# Revit family: REVIT-TPO
name_source: partatom
category: Mechanical Equipment
revit_build: Autodesk Revit 2017 (Build: 20190507_1515(x64)
units: mm (PartAtom-declared; Revit-internal decimal feet)

## family parameters
Always vertical = Yes
Cut with Voids When Loaded = No
Part Type = Normal
Room Calculation Point = No
Round Connector Dimension = Use Radius
Shared = No
Work Plane-Based = No

## types (39) — shared parameters
A = 8 3/8"
Air Inlet Depth = 3 1/8"
Air Inlet Extension = 18 15/16"
Air Inlet Width = 6 3/8"
Air Inlet X = 14 7/8"
Air Inlet Y = 5 1/4"
Air Inlet Y Offset = 2 1/16"
Air Inlet Z Offset = 2 1/16"
Assembly Code = D3040400
B = 3 15/16"
Burner Depth = 15 1/2"
Burner Height = 13 3/4"
Burner Width = 14 11/16"
Description = PVI Turbopower - Water Heater
Disclaimer = This rendering is for building modeling purposes only. Submittal/catalog is still the contract document. PVI reserves the right to change design and specification without notice.
Drain Angle = 0.00°
Energy Radius = 14 1/2"
Flue Collector Radius = 11 1/4"
Flue Extension = 18 1/4"
Manufacturer = PVI Industries, LLC
Oil Conn Angle = 90.00°
Oil Inlet NPT = 1/2"
Oil Inlet Radius = 1/4"
Oil Inlet X = 6 15/16"
Oil Inlet Y = 4 5/16"
Oil Inlet Z = 11"
Oil Pump Angle = 0.00°
Rear Access Extension = 0"
Relief Angle = 45.00°
Relief Valve NPT = 3/4"
Relief Valve Radius = 3/8"
URL = www.pvi.com
Voltage = 120 V

## per-type parameters (varying)
- 1500 L 1500A-TPO: Air Inlet Diameter=8"; Air Inlet Radius=4"; Cold Water Extension=38 1/2"; Cold Water NPT=3"; Cold Water Radius=1 1/2"; Control Panel Extension=44 1/2"; Drain Extension=41 3/8"; Drain NPT=1 1/2"; Drain Radius=3/4"; Enclosure Location=30"; Energy Extension=44 1/2"; FC OAL=60"; Flat Side Distance=75"; Flue Collector Extension=15 1/2"; Flue Diameter=8"; Flue Location=52 1/4"; Flue Radius=4"; Front Skid Extension=112 1/2"; Height to Cold Inlet=20"; Height to Drain=2 1/4"; Height to Energy=32 3/8"; Height to Hot Outlet=84 1/2"; Height to Relief=85 1/8"; Hot Outlet Angle=90.00°; Hot Water Extension=38 1/2"; Hot Water NPT=3"; Hot Water Radius=1 1/2"; Input Btu/h=1200000; Input gph Fuel Oil=8.6; Rear Skid Extension=37 1/2"; Recovery Rate 40F to 140F=1200 gph; Relief Extension=40 1/2"; Skid Center Dist=21 1/2"; Skid Length=75"; Skid Spacing=43"; Unit Height=104 1/2"; Unit Radius=37 1/2"
- 1250 L 1500A-TPO: Air Inlet Diameter=8"; Air Inlet Radius=4"; Cold Water Extension=38 1/2"; Cold Water NPT=3"; Cold Water Radius=1 1/2"; Control Panel Extension=44 1/2"; Drain Extension=41 3/8"; Drain NPT=1 1/2"; Drain Radius=3/4"; Enclosure Location=30"; Energy Extension=44 1/2"; FC OAL=60"; Flat Side Distance=75"; Flue Collector Extension=15 1/2"; Flue Diameter=8"; Flue Location=52 1/4"; Flue Radius=4"; Front Skid Extension=112 1/2"; Height to Cold Inlet=20"; Height to Drain=2 1/4"; Height to Energy=32 3/8"; Height to Hot Outlet=84 1/2"; Height to Relief=85 1/8"; Hot Outlet Angle=90.00°; Hot Water Extension=38 1/2"; Hot Water NPT=3"; Hot Water Radius=1 1/2"; Input Btu/h=1000000; Input gph Fuel Oil=7.2; Rear Skid Extension=37 1/2"; Recovery Rate 40F to 140F=1000 gph; Relief Extension=40 1/2"; Skid Center Dist=21 1/2"; Skid Length=75"; Skid Spacing=43"; Unit Height=104 1/2"; Unit Radius=37 1/2"
- 1000 L 1500A-TPO: Air Inlet Diameter=8"; Air Inlet Radius=4"; Cold Water Extension=38 1/2"; Cold Water NPT=3"; Cold Water Radius=1 1/2"; Control Panel Extension=44 1/2"; Drain Extension=41 3/8"; Drain NPT=1 1/2"; Drain Radius=3/4"; Enclosure Location=30"; Energy Extension=43 3/4"; FC OAL=52"; Flat Side Distance=75"; Flue Collector Extension=8 1/4"; Flue Diameter=8"; Flue Location=47 7/8"; Flue Radius=4"; Front Skid Extension=112 1/2"; Height to Cold Inlet=20"; Height to Drain=2 1/4"; Height to Energy=32 3/8"; Height to Hot Outlet=84 1/2"; Height to Relief=85 1/8"; Hot Outlet Angle=90.00°; Hot Water Extension=38 1/2"; Hot Water NPT=3"; Hot Water Radius=1 1/2"; Input Btu/h=800000; Input gph Fuel Oil=5.7; Rear Skid Extension=37 1/2"; Recovery Rate 40F to 140F=800 gph; Relief Extension=40 1/2"; Skid Center Dist=21 1/2"; Skid Length=75"; Skid Spacing=43"; Unit Height=104 1/2"; Unit Radius=37 1/2"
- 750 L 1500A-TPO: Air Inlet Diameter=6"; Air Inlet Radius=3"; Cold Water Extension=38 1/2"; Cold Water NPT=3"; Cold Water Radius=1 1/2"; Control Panel Extension=44 1/2"; Drain Extension=41 3/8"; Drain NPT=1 1/2"; Drain Radius=3/4"; Enclosure Location=30"; Energy Extension=43 3/4"; FC OAL=52"; Flat Side Distance=75"; Flue Collector Extension=8 1/4"; Flue Diameter=6"; Flue Location=47 7/8"; Flue Radius=3"; Front Skid Extension=112 1/2"; Height to Cold Inlet=20"; Height to Drain=2 1/4"; Height to Energy=32 3/8"; Height to Hot Outlet=84 1/2"; Height to Relief=85 1/8"; Hot Outlet Angle=90.00°; Hot Water Extension=38 1/2"; Hot Water NPT=3"; Hot Water Radius=1 1/2"; Input Btu/h=600000; Input gph Fuel Oil=4.3; Rear Skid Extension=37 1/2"; Recovery Rate 40F to 140F=600 gph; Relief Extension=40 1/2"; Skid Center Dist=21 1/2"; Skid Length=75"; Skid Spacing=43"; Unit Height=104 1/2"; Unit Radius=37 1/2"
- 500 L 1500A-TPO: Air Inlet Diameter=5"; Air Inlet Radius=2 1/2"; Cold Water Extension=38 1/2"; Cold Water NPT=3"; Cold Water Radius=1 1/2"; Control Panel Extension=44 1/2"; Drain Extension=41 3/8"; Drain NPT=1 1/2"; Drain Radius=3/4"; Enclosure Location=30"; Energy Extension=44 3/4"; FC OAL=50"; Flat Side Distance=75"; Flue Collector Extension=5 1/4"; Flue Diameter=5"; Flue Location=47 3/8"; Flue Radius=2 1/2"; Front Skid Extension=112 1/2"; Height to Cold Inlet=20"; Height to Drain=2 1/4"; Height to Energy=32 3/8"; Height to Hot Outlet=84 1/2"; Height to Relief=85 1/8"; Hot Outlet Angle=90.00°; Hot Water Extension=38 1/2"; Hot Water NPT=3"; Hot Water Radius=1 1/2"; Input Btu/h=399000; Input gph Fuel Oil=2.8; Rear Skid Extension=37 1/2"; Recovery Rate 40F to 140F=400 gph; Relief Extension=40 1/2"; Skid Center Dist=21 1/2"; Skid Length=75"; Skid Spacing=43"; Unit Height=104 1/2"; Unit Radius=37 1/2"
- 1500 L 1250A-TPO: Air Inlet Diameter=8"; Air Inlet Radius=4"; Cold Water Extension=38 1/2"; Cold Water NPT=3"; Cold Water Radius=1 1/2"; Control Panel Extension=44 1/2"; Drain Extension=41 3/8"; Drain NPT=1 1/2"; Drain Radius=3/4"; Enclosure Location=18"; Energy Extension=44 1/2"; FC OAL=60"; Flat Side Distance=75"; Flue Collector Extension=15 1/2"; Flue Diameter=8"; Flue Location=52 1/4"; Flue Radius=4"; Front Skid Extension=112 1/2"; Height to Cold Inlet=20"; Height to Drain=2 1/4"; Height to Energy=32 3/8"; Height to Hot Outlet=72 1/2"; Height to Relief=73 1/8"; Hot Outlet Angle=90.00°; Hot Water Extension=38 1/2"; Hot Water NPT=3"; Hot Water Radius=1 1/2"; Input Btu/h=1200000; Input gph Fuel Oil=8.6; Rear Skid Extension=37 1/2"; Recovery Rate 40F to 140F=1200 gph; Relief Extension=40 1/2"; Skid Center Dist=21 1/2"; Skid Length=75"; Skid Spacing=43"; Unit Height=92 1/2"; Unit Radius=37 1/2"
- 1250 L 1250A-TPO: Air Inlet Diameter=8"; Air Inlet Radius=4"; Cold Water Extension=38 1/2"; Cold Water NPT=3"; Cold Water Radius=1 1/2"; Control Panel Extension=44 1/2"; Drain Extension=41 3/8"; Drain NPT=1 1/2"; Drain Radius=3/4"; Enclosure Location=18"; Energy Extension=44 1/2"; FC OAL=60"; Flat Side Distance=75"; Flue Collector Extension=15 1/2"; Flue Diameter=8"; Flue Location=52 1/4"; Flue Radius=4"; Front Skid Extension=112 1/2"; Height to Cold Inlet=20"; Height to Drain=2 1/4"; Height to Energy=32 3/8"; Height to Hot Outlet=72 1/2"; Height to Relief=73 1/8"; Hot Outlet Angle=90.00°; Hot Water Extension=38 1/2"; Hot Water NPT=3"; Hot Water Radius=1 1/2"; Input Btu/h=1000000; Input gph Fuel Oil=7.2; Rear Skid Extension=37 1/2"; Recovery Rate 40F to 140F=1000 gph; Relief Extension=40 1/2"; Skid Center Dist=21 1/2"; Skid Length=75"; Skid Spacing=43"; Unit Height=92 1/2"; Unit Radius=37 1/2"
- 1000 L 1250A-TPO: Air Inlet Diameter=8"; Air Inlet Radius=4"; Cold Water Extension=38 1/2"; Cold Water NPT=3"; Cold Water Radius=1 1/2"; Control Panel Extension=44 1/2"; Drain Extension=41 3/8"; Drain NPT=1 1/2"; Drain Radius=3/4"; Enclosure Location=18"; Energy Extension=43 3/4"; FC OAL=52"; Flat Side Distance=75"; Flue Collector Extension=8 1/4"; Flue Diameter=8"; Flue Location=47 7/8"; Flue Radius=4"; Front Skid Extension=112 1/2"; Height to Cold Inlet=20"; Height to Drain=2 1/4"; Height to Energy=32 3/8"; Height to Hot Outlet=72 1/2"; Height to Relief=73 1/8"; Hot Outlet Angle=90.00°; Hot Water Extension=38 1/2"; Hot Water NPT=3"; Hot Water Radius=1 1/2"; Input Btu/h=800000; Input gph Fuel Oil=5.7; Rear Skid Extension=37 1/2"; Recovery Rate 40F to 140F=800 gph; Relief Extension=40 1/2"; Skid Center Dist=21 1/2"; Skid Length=75"; Skid Spacing=43"; Unit Height=92 1/2"; Unit Radius=37 1/2"
- 750 L 1250A-TPO: Air Inlet Diameter=6"; Air Inlet Radius=3"; Cold Water Extension=38 1/2"; Cold Water NPT=3"; Cold Water Radius=1 1/2"; Control Panel Extension=44 1/2"; Drain Extension=41 3/8"; Drain NPT=1 1/2"; Drain Radius=3/4"; Enclosure Location=18"; Energy Extension=43 3/4"; FC OAL=52"; Flat Side Distance=75"; Flue Collector Extension=8 1/4"; Flue Diameter=6"; Flue Location=47 7/8"; Flue Radius=3"; Front Skid Extension=112 1/2"; Height to Cold Inlet=20"; Height to Drain=2 1/4"; Height to Energy=32 3/8"; Height to Hot Outlet=72 1/2"; Height to Relief=73 1/8"; Hot Outlet Angle=90.00°; Hot Water Extension=38 1/2"; Hot Water NPT=3"; Hot Water Radius=1 1/2"; Input Btu/h=600000; Input gph Fuel Oil=4.3; Rear Skid Extension=37 1/2"; Recovery Rate 40F to 140F=600 gph; Relief Extension=40 1/2"; Skid Center Dist=21 1/2"; Skid Length=75"; Skid Spacing=43"; Unit Height=92 1/2"; Unit Radius=37 1/2"
- 500 L 1250A-TPO: Air Inlet Diameter=5"; Air Inlet Radius=2 1/2"; Cold Water Extension=38 1/2"; Cold Water NPT=3"; Cold Water Radius=1 1/2"; Control Panel Extension=44 1/2"; Drain Extension=41 3/8"; Drain NPT=1 1/2"; Drain Radius=3/4"; Enclosure Location=18"; Energy Extension=44 3/4"; FC OAL=50"; Flat Side Distance=75"; Flue Collector Extension=5 1/4"; Flue Diameter=5"; Flue Location=47 3/8"; Flue Radius=2 1/2"; Front Skid Extension=112 1/2"; Height to Cold Inlet=20"; Height to Drain=2 1/4"; Height to Energy=32 3/8"; Height to Hot Outlet=72 1/2"; Height to Relief=73 1/8"; Hot Outlet Angle=90.00°; Hot Water Extension=38 1/2"; Hot Water NPT=3"; Hot Water Radius=1 1/2"; Input Btu/h=399000; Input gph Fuel Oil=2.8; Rear Skid Extension=37 1/2"; Recovery Rate 40F to 140F=400 gph; Relief Extension=40 1/2"; Skid Center Dist=21 1/2"; Skid Length=75"; Skid Spacing=43"; Unit Height=92 1/2"; Unit Radius=37 1/2"
- 1500 L 900A-TPO: Air Inlet Diameter=8"; Air Inlet Radius=4"; Cold Water Extension=34 1/4"; Cold Water NPT=3"; Cold Water Radius=1 1/2"; Control Panel Extension=40 1/4"; Drain Extension=37 1/8"; Drain NPT=1 1/2"; Drain Radius=3/4"; Enclosure Location=24"; Energy Extension=39"; FC OAL=54 1/2"; Flat Side Distance=66 1/2"; Flue Collector Extension=15 1/2"; Flue Diameter=8"; Flue Location=46 3/4"; Flue Radius=4"; Front Skid Extension=101 1/4"; Height to Cold Inlet=20 3/8"; Height to Drain=2 1/4"; Height to Energy=32 5/8"; Height to Hot Outlet=72 7/8"; Height to Relief=73 1/2"; Hot Outlet Angle=90.00°; Hot Water Extension=34 1/4"; Hot Water NPT=3"; Hot Water Radius=1 1/2"; Input Btu/h=1200000; Input gph Fuel Oil=8.6; Rear Skid Extension=33 1/4"; Recovery Rate 40F to 140F=1200 gph; Relief Extension=36 1/4"; Skid Center Dist=18"; Skid Length=68"; Skid Spacing=36"; Unit Height=93 1/4"; Unit Radius=33 1/4"
- 1250 L 900A-TPO: Air Inlet Diameter=8"; Air Inlet Radius=4"; Cold Water Extension=34 1/4"; Cold Water NPT=3"; Cold Water Radius=1 1/2"; Control Panel Extension=40 1/4"; Drain Extension=37 1/8"; Drain NPT=1 1/2"; Drain Radius=3/4"; Enclosure Location=24"; Energy Extension=39"; FC OAL=54 1/2"; Flat Side Distance=66 1/2"; Flue Collector Extension=15 1/2"; Flue Diameter=8"; Flue Location=46 3/4"; Flue Radius=4"; Front Skid Extension=101 1/4"; Height to Cold Inlet=20 3/8"; Height to Drain=2 1/4"; Height to Energy=32 5/8"; Height to Hot Outlet=72 7/8"; Height to Relief=73 1/2"; Hot Outlet Angle=90.00°; Hot Water Extension=34 1/4"; Hot Water NPT=3"; Hot Water Radius=1 1/2"; Input Btu/h=1000000; Input gph Fuel Oil=7.2; Rear Skid Extension=33 1/4"; Recovery Rate 40F to 140F=1000 gph; Relief Extension=36 1/4"; Skid Center Dist=18"; Skid Length=68"; Skid Spacing=36"; Unit Height=93 1/4"; Unit Radius=33 1/4"
- 1000 L 900A-TPO: Air Inlet Diameter=8"; Air Inlet Radius=4"; Cold Water Extension=34 1/4"; Cold Water NPT=3"; Cold Water Radius=1 1/2"; Control Panel Extension=40 1/4"; Drain Extension=37 1/8"; Drain NPT=1 1/2"; Drain Radius=3/4"; Enclosure Location=24"; Energy Extension=38 1/4"; FC OAL=46 1/2"; Flat Side Distance=66 1/2"; Flue Collector Extension=8 1/4"; Flue Diameter=8"; Flue Location=42 3/8"; Flue Radius=4"; Front Skid Extension=101 1/4"; Height to Cold Inlet=20 3/8"; Height to Drain=2 1/4"; Height to Energy=32 5/8"; Height to Hot Outlet=72 7/8"; Height to Relief=73 1/2"; Hot Outlet Angle=90.00°; Hot Water Extension=34 1/4"; Hot Water NPT=3"; Hot Water Radius=1 1/2"; Input Btu/h=800000; Input gph Fuel Oil=5.7; Rear Skid Extension=33 1/4"; Recovery Rate 40F to 140F=800 gph; Relief Extension=36 1/4"; Skid Center Dist=18"; Skid Length=68"; Skid Spacing=36"; Unit Height=93 1/4"; Unit Radius=33 1/4"
- 750 L 900A-TPO: Air Inlet Diameter=6"; Air Inlet Radius=3"; Cold Water Extension=34 1/4"; Cold Water NPT=3"; Cold Water Radius=1 1/2"; Control Panel Extension=40 1/4"; Drain Extension=37 1/8"; Drain NPT=1 1/2"; Drain Radius=3/4"; Enclosure Location=24"; Energy Extension=38 1/4"; FC OAL=46 1/2"; Flat Side Distance=66 1/2"; Flue Collector Extension=8 1/4"; Flue Diameter=6"; Flue Location=42 3/8"; Flue Radius=3"; Front Skid Extension=101 1/4"; Height to Cold Inlet=20 3/8"; Height to Drain=2 1/4"; Height to Energy=32 5/8"; Height to Hot Outlet=72 7/8"; Height to Relief=73 1/2"; Hot Outlet Angle=90.00°; Hot Water Extension=34 1/4"; Hot Water NPT=3"; Hot Water Radius=1 1/2"; Input Btu/h=600000; Input gph Fuel Oil=4.3; Rear Skid Extension=33 1/4"; Recovery Rate 40F to 140F=600 gph; Relief Extension=36 1/4"; Skid Center Dist=18"; Skid Length=68"; Skid Spacing=36"; Unit Height=93 1/4"; Unit Radius=33 1/4"
- 500 L 900A-TPO: Air Inlet Diameter=5"; Air Inlet Radius=2 1/2"; Cold Water Extension=34 1/4"; Cold Water NPT=3"; Cold Water Radius=1 1/2"; Control Panel Extension=40 1/4"; Drain Extension=37 1/8"; Drain NPT=1 1/2"; Drain Radius=3/4"; Enclosure Location=24"; Energy Extension=38 1/4"; FC OAL=43 1/2"; Flat Side Distance=66 1/2"; Flue Collector Extension=5 1/4"; Flue Diameter=5"; Flue Location=40 7/8"; Flue Radius=2 1/2"; Front Skid Extension=101 1/4"; Height to Cold Inlet=20 3/8"; Height to Drain=2 1/4"; Height to Energy=32 5/8"; Height to Hot Outlet=72 7/8"; Height to Relief=73 1/2"; Hot Outlet Angle=90.00°; Hot Water Extension=34 1/4"; Hot Water NPT=3"; Hot Water Radius=1 1/2"; Input Btu/h=399000; Input gph Fuel Oil=2.8; Rear Skid Extension=33 1/4"; Recovery Rate 40F to 140F=400 gph; Relief Extension=36 1/4"; Skid Center Dist=18"; Skid Length=68"; Skid Spacing=36"; Unit Height=93 1/4"; Unit Radius=33 1/4"
- 1500 L 600A-TPO: Air Inlet Diameter=8"; Air Inlet Radius=4"; Cold Water Extension=28 7/8"; Cold Water NPT=3"; Cold Water Radius=1 1/2"; Control Panel Extension=34 7/8"; Drain Extension=31 3/4"; Drain NPT=1 1/2"; Drain Radius=3/4"; Enclosure Location=19 1/2"; Energy Extension=33 3/8"; FC OAL=48 7/8"; Flat Side Distance=55 3/4"; Flue Collector Extension=15 1/2"; Flue Diameter=8"; Flue Location=41 1/8"; Flue Radius=4"; Front Skid Extension=82 3/8"; Height to Cold Inlet=18 1/4"; Height to Drain=2 1/4"; Height to Energy=30"; Height to Hot Outlet=69 3/8"; Height to Relief=70"; Hot Outlet Angle=90.00°; Hot Water Extension=28 7/8"; Hot Water NPT=3"; Hot Water Radius=1 1/2"; Input Btu/h=1200000; Input gph Fuel Oil=8.6; Rear Skid Extension=27 7/8"; Recovery Rate 40F to 140F=1200 gph; Relief Extension=30 7/8"; Skid Center Dist=13 1/2"; Skid Length=54 1/2"; Skid Spacing=27"; Unit Height=87 3/4"; Unit Radius=27 7/8"
- 1250 L 600A-TPO: Air Inlet Diameter=8"; Air Inlet Radius=4"; Cold Water Extension=28 7/8"; Cold Water NPT=3"; Cold Water Radius=1 1/2"; Control Panel Extension=34 7/8"; Drain Extension=31 3/4"; Drain NPT=1 1/2"; Drain Radius=3/4"; Enclosure Location=19 1/2"; Energy Extension=33 3/8"; FC OAL=48 7/8"; Flat Side Distance=55 3/4"; Flue Collector Extension=15 1/2"; Flue Diameter=8"; Flue Location=41 1/8"; Flue Radius=4"; Front Skid Extension=82 3/8"; Height to Cold Inlet=18 1/4"; Height to Drain=2 1/4"; Height to Energy=30"; Height to Hot Outlet=69 3/8"; Height to Relief=70"; Hot Outlet Angle=90.00°; Hot Water Extension=28 7/8"; Hot Water NPT=3"; Hot Water Radius=1 1/2"; Input Btu/h=1000000; Input gph Fuel Oil=7.2; Rear Skid Extension=27 7/8"; Recovery Rate 40F to 140F=1000 gph; Relief Extension=30 7/8"; Skid Center Dist=13 1/2"; Skid Length=54 1/2"; Skid Spacing=27"; Unit Height=87 3/4"; Unit Radius=27 7/8"
- 1000 L 600A-TPO: Air Inlet Diameter=8"; Air Inlet Radius=4"; Cold Water Extension=28 7/8"; Cold Water NPT=3"; Cold Water Radius=1 1/2"; Control Panel Extension=34 7/8"; Drain Extension=31 3/4"; Drain NPT=1 1/2"; Drain Radius=3/4"; Enclosure Location=19 1/2"; Energy Extension=32 5/8"; FC OAL=40 7/8"; Flat Side Distance=55 3/4"; Flue Collector Extension=8 1/4"; Flue Diameter=8"; Flue Location=36 3/4"; Flue Radius=4"; Front Skid Extension=82 3/8"; Height to Cold Inlet=18 1/4"; Height to Drain=2 1/4"; Height to Energy=30"; Height to Hot Outlet=69 3/8"; Height to Relief=70"; Hot Outlet Angle=90.00°; Hot Water Extension=28 7/8"; Hot Water NPT=3"; Hot Water Radius=1 1/2"; Input Btu/h=800000; Input gph Fuel Oil=5.7; Rear Skid Extension=27 7/8"; Recovery Rate 40F to 140F=800 gph; Relief Extension=30 7/8"; Skid Center Dist=13 1/2"; Skid Length=54 1/2"; Skid Spacing=27"; Unit Height=87 3/4"; Unit Radius=27 7/8"
- 750 L 600A-TPO: Air Inlet Diameter=6"; Air Inlet Radius=3"; Cold Water Extension=28 7/8"; Cold Water NPT=3"; Cold Water Radius=1 1/2"; Control Panel Extension=34 7/8"; Drain Extension=31 3/4"; Drain NPT=1 1/2"; Drain Radius=3/4"; Enclosure Location=19 1/2"; Energy Extension=32 5/8"; FC OAL=40 7/8"; Flat Side Distance=55 3/4"; Flue Collector Extension=8 1/4"; Flue Diameter=6"; Flue Location=36 3/4"; Flue Radius=3"; Front Skid Extension=82 3/8"; Height to Cold Inlet=18 1/4"; Height to Drain=2 1/4"; Height to Energy=30"; Height to Hot Outlet=69 3/8"; Height to Relief=70"; Hot Outlet Angle=90.00°; Hot Water Extension=28 7/8"; Hot Water NPT=3"; Hot Water Radius=1 1/2"; Input Btu/h=600000; Input gph Fuel Oil=4.3; Rear Skid Extension=27 7/8"; Recovery Rate 40F to 140F=600 gph; Relief Extension=30 7/8"; Skid Center Dist=13 1/2"; Skid Length=54 1/2"; Skid Spacing=27"; Unit Height=87 3/4"; Unit Radius=27 7/8"
- 500 L 600A-TPO: Air Inlet Diameter=5"; Air Inlet Radius=2 1/2"; Cold Water Extension=28 7/8"; Cold Water NPT=3"; Cold Water Radius=1 1/2"; Control Panel Extension=34 7/8"; Drain Extension=31 3/4"; Drain NPT=1 1/2"; Drain Radius=3/4"; Enclosure Location=19 1/2"; Energy Extension=32 5/8"; FC OAL=37 7/8"; Flat Side Distance=55 3/4"; Flue Collector Extension=5 1/4"; Flue Diameter=5"; Flue Location=35 1/4"; Flue Radius=2 1/2"; Front Skid Extension=82 3/8"; Height to Cold Inlet=18 1/4"; Height to Drain=2 1/4"; Height to Energy=30"; Height to Hot Outlet=69 3/8"; Height to Relief=70"; Hot Outlet Angle=90.00°; Hot Water Extension=28 7/8"; Hot Water NPT=3"; Hot Water Radius=1 1/2"; Input Btu/h=399000; Input gph Fuel Oil=2.8; Rear Skid Extension=27 7/8"; Recovery Rate 40F to 140F=400 gph; Relief Extension=30 7/8"; Skid Center Dist=13 1/2"; Skid Length=54 1/2"; Skid Spacing=27"; Unit Height=87 3/4"; Unit Radius=27 7/8"
- 1500 L 400A-TPO: Air Inlet Diameter=8"; Air Inlet Radius=4"; Cold Water Extension=23 5/8"; Cold Water NPT=2"; Cold Water Radius=1"; Control Panel Extension=29 5/8"; Drain Extension=26 1/2"; Drain NPT=1"; Drain Radius=1/2"; Enclosure Location=15"; Energy Extension=38 1/8"; FC OAL=53 5/8"; Flat Side Distance=45 1/4"; Flue Collector Extension=15 1/2"; Flue Diameter=8"; Flue Location=45 7/8"; Flue Radius=4"; Front Skid Extension=77 1/8"; Height to Cold Inlet=17 1/16"; Height to Drain=1 7/8"; Height to Energy=28 3/4"; Height to Hot Outlet=68 1/2"; Height to Relief=69 1/8"; Hot Outlet Angle=90.00°; Hot Water Extension=23 5/8"; Hot Water NPT=2"; Hot Water Radius=1"; Input Btu/h=1200000; Input gph Fuel Oil=8.6; Rear Skid Extension=22 5/8"; Recovery Rate 40F to 140F=1200 gph; Relief Extension=25 5/8"; Skid Center Dist=13 1/2"; Skid Length=54 1/2"; Skid Spacing=27"; Unit Height=85 1/2"; Unit Radius=22 5/8"
- 1250 L 400A-TPO: Air Inlet Diameter=8"; Air Inlet Radius=4"; Cold Water Extension=23 5/8"; Cold Water NPT=2"; Cold Water Radius=1"; Control Panel Extension=29 5/8"; Drain Extension=26 1/2"; Drain NPT=1"; Drain Radius=1/2"; Enclosure Location=15"; Energy Extension=38 1/8"; FC OAL=53 5/8"; Flat Side Distance=45 1/4"; Flue Collector Extension=15 1/2"; Flue Diameter=8"; Flue Location=45 7/8"; Flue Radius=4"; Front Skid Extension=77 1/8"; Height to Cold Inlet=17 1/16"; Height to Drain=1 7/8"; Height to Energy=28 3/4"; Height to Hot Outlet=68 1/2"; Height to Relief=69 1/8"; Hot Outlet Angle=90.00°; Hot Water Extension=23 5/8"; Hot Water NPT=2"; Hot Water Radius=1"; Input Btu/h=1000000; Input gph Fuel Oil=7.2; Rear Skid Extension=22 5/8"; Recovery Rate 40F to 140F=1000 gph; Relief Extension=25 5/8"; Skid Center Dist=13 1/2"; Skid Length=54 1/2"; Skid Spacing=27"; Unit Height=85 1/2"; Unit Radius=22 5/8"
- 1000 L 400A-TPO: Air Inlet Diameter=8"; Air Inlet Radius=4"; Cold Water Extension=23 5/8"; Cold Water NPT=2"; Cold Water Radius=1"; Control Panel Extension=29 5/8"; Drain Extension=26 1/2"; Drain NPT=1"; Drain Radius=1/2"; Enclosure Location=15"; Energy Extension=27 1/8"; FC OAL=35 3/8"; Flat Side Distance=45 1/4"; Flue Collector Extension=8 1/4"; Flue Diameter=8"; Flue Location=31 1/4"; Flue Radius=4"; Front Skid Extension=68 5/8"; Height to Cold Inlet=17 1/16"; Height to Drain=1 7/8"; Height to Energy=28 3/4"; Height to Hot Outlet=68 1/2"; Height to Relief=69 1/8"; Hot Outlet Angle=90.00°; Hot Water Extension=23 5/8"; Hot Water NPT=2"; Hot Water Radius=1"; Input Btu/h=800000; Input gph Fuel Oil=5.7; Rear Skid Extension=22 5/8"; Recovery Rate 40F to 140F=800 gph; Relief Extension=25 5/8"; Skid Center Dist=13 1/2"; Skid Length=46"; Skid Spacing=27"; Unit Height=85 1/2"; Unit Radius=22 5/8"
- 750 L 400A-TPO: Air Inlet Diameter=6"; Air Inlet Radius=3"; Cold Water Extension=23 5/8"; Cold Water NPT=2"; Cold Water Radius=1"; Control Panel Extension=29 5/8"; Drain Extension=26 1/2"; Drain NPT=1"; Drain Radius=1/2"; Enclosure Location=15"; Energy Extension=27 1/8"; FC OAL=35 3/8"; Flat Side Distance=45 1/4"; Flue Collector Extension=8 1/4"; Flue Diameter=6"; Flue Location=31 1/4"; Flue Radius=3"; Front Skid Extension=68 5/8"; Height to Cold Inlet=17 1/16"; Height to Drain=1 7/8"; Height to Energy=28 3/4"; Height to Hot Outlet=68 1/2"; Height to Relief=69 1/8"; Hot Outlet Angle=90.00°; Hot Water Extension=23 5/8"; Hot Water NPT=2"; Hot Water Radius=1"; Input Btu/h=600000; Input gph Fuel Oil=4.3; Rear Skid Extension=22 5/8"; Recovery Rate 40F to 140F=600 gph; Relief Extension=25 5/8"; Skid Center Dist=13 1/2"; Skid Length=46"; Skid Spacing=27"; Unit Height=85 1/2"; Unit Radius=22 5/8"
- 500 L 400A-TPO: Air Inlet Diameter=5"; Air Inlet Radius=2 1/2"; Cold Water Extension=23 5/8"; Cold Water NPT=2"; Cold Water Radius=1"; Control Panel Extension=29 5/8"; Drain Extension=26 1/2"; Drain NPT=1"; Drain Radius=1/2"; Enclosure Location=15"; Energy Extension=27 1/8"; FC OAL=32 3/8"; Flat Side Distance=45 1/4"; Flue Collector Extension=5 1/4"; Flue Diameter=5"; Flue Location=29 3/4"; Flue Radius=2 1/2"; Front Skid Extension=68 5/8"; Height to Cold Inlet=17 1/16"; Height to Drain=1 7/8"; Height to Energy=28 3/4"; Height to Hot Outlet=68 1/2"; Height to Relief=69 1/8"; Hot Outlet Angle=90.00°; Hot Water Extension=23 5/8"; Hot Water NPT=2"; Hot Water Radius=1"; Input Btu/h=399000; Input gph Fuel Oil=2.8; Rear Skid Extension=22 5/8"; Recovery Rate 40F to 140F=400 gph; Relief Extension=25 5/8"; Skid Center Dist=13 1/2"; Skid Length=46"; Skid Spacing=27"; Unit Height=85 1/2"; Unit Radius=22 5/8"
- 1500 L 250A-TPO: Air Inlet Diameter=8"; Air Inlet Radius=4"; Cold Water Extension=23 5/8"; Cold Water NPT=2"; Cold Water Radius=1"; Control Panel Extension=29 5/8"; Drain Extension=26 1/2"; Drain NPT=1"; Drain Radius=1/2"; Enclosure Location=1 1/2"; Energy Extension=38 1/8"; FC OAL=53 5/8"; Flat Side Distance=45 1/4"; Flue Collector Extension=15 1/2"; Flue Diameter=8"; Flue Location=45 7/8"; Flue Radius=4"; Front Skid Extension=77 1/8"; Height to Cold Inlet=17 1/16"; Height to Drain=1 7/8"; Height to Energy=28 3/4"; Height to Hot Outlet=38 7/8"; Height to Relief=45 1/8"; Hot Outlet Angle=0.00°; Hot Water Extension=23 5/8"; Hot Water NPT=2"; Hot Water Radius=1"; Input Btu/h=1200000; Input gph Fuel Oil=8.6; Rear Skid Extension=22 5/8"; Recovery Rate 40F to 140F=1200 gph; Relief Extension=25 5/8"; Skid Center Dist=13 1/2"; Skid Length=54 1/2"; Skid Spacing=27"; Unit Height=61 1/2"; Unit Radius=22 5/8"
- 1250 L 250A-TPO: Air Inlet Diameter=8"; Air Inlet Radius=4"; Cold Water Extension=23 5/8"; Cold Water NPT=2"; Cold Water Radius=1"; Control Panel Extension=29 5/8"; Drain Extension=26 1/2"; Drain NPT=1"; Drain Radius=1/2"; Enclosure Location=1 1/2"; Energy Extension=38 1/8"; FC OAL=53 5/8"; Flat Side Distance=45 1/4"; Flue Collector Extension=15 1/2"; Flue Diameter=8"; Flue Location=45 7/8"; Flue Radius=4"; Front Skid Extension=77 1/8"; Height to Cold Inlet=17 1/16"; Height to Drain=1 7/8"; Height to Energy=28 3/4"; Height to Hot Outlet=38 7/8"; Height to Relief=45 1/8"; Hot Outlet Angle=0.00°; Hot Water Extension=23 5/8"; Hot Water NPT=2"; Hot Water Radius=1"; Input Btu/h=1000000; Input gph Fuel Oil=7.2; Rear Skid Extension=22 5/8"; Recovery Rate 40F to 140F=1000 gph; Relief Extension=25 5/8"; Skid Center Dist=13 1/2"; Skid Length=54 1/2"; Skid Spacing=27"; Unit Height=61 1/2"; Unit Radius=22 5/8"
- 1000 L 250A-TPO: Air Inlet Diameter=8"; Air Inlet Radius=4"; Cold Water Extension=23 5/8"; Cold Water NPT=2"; Cold Water Radius=1"; Control Panel Extension=29 5/8"; Drain Extension=26 1/2"; Drain NPT=1"; Drain Radius=1/2"; Enclosure Location=1 1/2"; Energy Extension=27 1/8"; FC OAL=35 3/8"; Flat Side Distance=45 1/4"; Flue Collector Extension=8 1/4"; Flue Diameter=8"; Flue Location=31 1/4"; Flue Radius=4"; Front Skid Extension=68 5/8"; Height to Cold Inlet=17 1/16"; Height to Drain=1 7/8"; Height to Energy=28 3/4"; Height to Hot Outlet=38 7/8"; Height to Relief=45 1/8"; Hot Outlet Angle=0.00°; Hot Water Extension=23 5/8"; Hot Water NPT=2"; Hot Water Radius=1"; Input Btu/h=800000; Input gph Fuel Oil=5.7; Rear Skid Extension=22 5/8"; Recovery Rate 40F to 140F=800 gph; Relief Extension=25 5/8"; Skid Center Dist=13 1/2"; Skid Length=46"; Skid Spacing=27"; Unit Height=61 1/2"; Unit Radius=22 5/8"
- 750 L 250A-TPO: Air Inlet Diameter=6"; Air Inlet Radius=3"; Cold Water Extension=23 5/8"; Cold Water NPT=2"; Cold Water Radius=1"; Control Panel Extension=29 5/8"; Drain Extension=26 1/2"; Drain NPT=1"; Drain Radius=1/2"; Enclosure Location=1 1/2"; Energy Extension=27 1/8"; FC OAL=35 3/8"; Flat Side Distance=45 1/4"; Flue Collector Extension=8 1/4"; Flue Diameter=6"; Flue Location=31 1/4"; Flue Radius=3"; Front Skid Extension=68 5/8"; Height to Cold Inlet=17 1/16"; Height to Drain=1 7/8"; Height to Energy=28 3/4"; Height to Hot Outlet=38 7/8"; Height to Relief=45 1/8"; Hot Outlet Angle=0.00°; Hot Water Extension=23 5/8"; Hot Water NPT=2"; Hot Water Radius=1"; Input Btu/h=600000; Input gph Fuel Oil=4.3; Rear Skid Extension=22 5/8"; Recovery Rate 40F to 140F=600 gph; Relief Extension=25 5/8"; Skid Center Dist=13 1/2"; Skid Length=46"; Skid Spacing=27"; Unit Height=61 1/2"; Unit Radius=22 5/8"
- 500 L 250A-TPO: Air Inlet Diameter=5"; Air Inlet Radius=2 1/2"; Cold Water Extension=23 5/8"; Cold Water NPT=2"; Cold Water Radius=1"; Control Panel Extension=29 5/8"; Drain Extension=26 1/2"; Drain NPT=1"; Drain Radius=1/2"; Enclosure Location=1 1/2"; Energy Extension=27 1/8"; FC OAL=32 3/8"; Flat Side Distance=45 1/4"; Flue Collector Extension=5 1/4"; Flue Diameter=5"; Flue Location=29 3/4"; Flue Radius=2 1/2"; Front Skid Extension=68 5/8"; Height to Cold Inlet=17 1/16"; Height to Drain=1 7/8"; Height to Energy=28 3/4"; Height to Hot Outlet=38 7/8"; Height to Relief=45 1/8"; Hot Outlet Angle=0.00°; Hot Water Extension=23 5/8"; Hot Water NPT=2"; Hot Water Radius=1"; Input Btu/h=399000; Input gph Fuel Oil=2.8; Rear Skid Extension=22 5/8"; Recovery Rate 40F to 140F=400 gph; Relief Extension=25 5/8"; Skid Center Dist=13 1/2"; Skid Length=46"; Skid Spacing=27"; Unit Height=61 1/2"; Unit Radius=22 5/8"
- 1000 L 215A-TPO: Air Inlet Diameter=8"; Air Inlet Radius=4"; Cold Water Extension=19 1/8"; Cold Water NPT=2"; Cold Water Radius=1"; Control Panel Extension=25 1/8"; Drain Extension=22"; Drain NPT=1"; Drain Radius=1/2"; Enclosure Location=11 3/4"; Energy Extension=37 1/8"; FC OAL=45 3/8"; Flat Side Distance=34"; Flue Collector Extension=8 1/4"; Flue Diameter=8"; Flue Location=41 1/4"; Flue Radius=4"; Front Skid Extension=55 1/8"; Height to Cold Inlet=14 13/16"; Height to Drain=1 7/8"; Height to Energy=26 1/2"; Height to Hot Outlet=64"; Height to Relief=66 5/16"; Hot Outlet Angle=90.00°; Hot Water Extension=19 1/8"; Hot Water NPT=2"; Hot Water Radius=1"; Input Btu/h=800000; Input gph Fuel Oil=5.7; Rear Skid Extension=18 1/8"; Recovery Rate 40F to 140F=800 gph; Relief Extension=21 1/8"; Skid Center Dist=8 1/2"; Skid Length=37"; Skid Spacing=17"; Unit Height=76"; Unit Radius=18 1/8"
- 750 L 215A-TPO: Air Inlet Diameter=6"; Air Inlet Radius=3"; Cold Water Extension=19 1/8"; Cold Water NPT=2"; Cold Water Radius=1"; Control Panel Extension=25 1/8"; Drain Extension=22"; Drain NPT=1"; Drain Radius=1/2"; Enclosure Location=11 3/4"; Energy Extension=37 1/8"; FC OAL=45 3/8"; Flat Side Distance=34"; Flue Collector Extension=8 1/4"; Flue Diameter=6"; Flue Location=41 1/4"; Flue Radius=3"; Front Skid Extension=55 1/8"; Height to Cold Inlet=14 13/16"; Height to Drain=1 7/8"; Height to Energy=26 1/2"; Height to Hot Outlet=64"; Height to Relief=66 5/16"; Hot Outlet Angle=90.00°; Hot Water Extension=19 1/8"; Hot Water NPT=2"; Hot Water Radius=1"; Input Btu/h=600000; Input gph Fuel Oil=4.3; Rear Skid Extension=18 1/8"; Recovery Rate 40F to 140F=600 gph; Relief Extension=21 1/8"; Skid Center Dist=8 1/2"; Skid Length=37"; Skid Spacing=17"; Unit Height=76"; Unit Radius=18 1/8"
- 500 L 215A-TPO: Air Inlet Diameter=5"; Air Inlet Radius=2 1/2"; Cold Water Extension=19 1/8"; Cold Water NPT=2"; Cold Water Radius=1"; Control Panel Extension=25 1/8"; Drain Extension=22"; Drain NPT=1"; Drain Radius=1/2"; Enclosure Location=11 3/4"; Energy Extension=23 1/8"; FC OAL=28 3/8"; Flat Side Distance=34"; Flue Collector Extension=5 1/4"; Flue Diameter=5"; Flue Location=25 3/4"; Flue Radius=2 1/2"; Front Skid Extension=55 1/8"; Height to Cold Inlet=14 13/16"; Height to Drain=1 7/8"; Height to Energy=26 1/2"; Height to Hot Outlet=64"; Height to Relief=66 5/16"; Hot Outlet Angle=90.00°; Hot Water Extension=19 1/8"; Hot Water NPT=2"; Hot Water Radius=1"; Input Btu/h=399000; Input gph Fuel Oil=2.8; Rear Skid Extension=18 1/8"; Recovery Rate 40F to 140F=400 gph; Relief Extension=21 1/8"; Skid Center Dist=8 1/2"; Skid Length=37"; Skid Spacing=17"; Unit Height=76"; Unit Radius=18 1/8"
- 1000 L 175A-TPO: Air Inlet Diameter=8"; Air Inlet Radius=4"; Cold Water Extension=19 1/8"; Cold Water NPT=2"; Cold Water Radius=1"; Control Panel Extension=25 1/8"; Drain Extension=22"; Drain NPT=1"; Drain Radius=1/2"; Enclosure Location=9 3/4"; Energy Extension=37 1/8"; FC OAL=45 3/8"; Flat Side Distance=34"; Flue Collector Extension=8 1/4"; Flue Diameter=8"; Flue Location=41 1/4"; Flue Radius=4"; Front Skid Extension=55 1/8"; Height to Cold Inlet=14 13/16"; Height to Drain=1 7/8"; Height to Energy=26 1/2"; Height to Hot Outlet=50 7/8"; Height to Relief=57 7/8"; Hot Outlet Angle=0.00°; Hot Water Extension=19 1/8"; Hot Water NPT=2"; Hot Water Radius=1"; Input Btu/h=800000; Input gph Fuel Oil=5.7; Rear Skid Extension=18 1/8"; Recovery Rate 40F to 140F=800 gph; Relief Extension=21 1/8"; Skid Center Dist=8 1/2"; Skid Length=37"; Skid Spacing=17"; Unit Height=69"; Unit Radius=18 1/8"
- 750 L 175A-TPO: Air Inlet Diameter=6"; Air Inlet Radius=3"; Cold Water Extension=19 1/8"; Cold Water NPT=2"; Cold Water Radius=1"; Control Panel Extension=25 1/8"; Drain Extension=22"; Drain NPT=1"; Drain Radius=1/2"; Enclosure Location=9 3/4"; Energy Extension=37 1/8"; FC OAL=45 3/8"; Flat Side Distance=34"; Flue Collector Extension=8 1/4"; Flue Diameter=6"; Flue Location=41 1/4"; Flue Radius=3"; Front Skid Extension=55 1/8"; Height to Cold Inlet=14 13/16"; Height to Drain=1 7/8"; Height to Energy=26 1/2"; Height to Hot Outlet=50 7/8"; Height to Relief=57 7/8"; Hot Outlet Angle=0.00°; Hot Water Extension=19 1/8"; Hot Water NPT=2"; Hot Water Radius=1"; Input Btu/h=600000; Input gph Fuel Oil=4.3; Rear Skid Extension=18 1/8"; Recovery Rate 40F to 140F=600 gph; Relief Extension=21 1/8"; Skid Center Dist=8 1/2"; Skid Length=37"; Skid Spacing=17"; Unit Height=69"; Unit Radius=18 1/8"
- 500 L 175A-TPO: Air Inlet Diameter=5"; Air Inlet Radius=2 1/2"; Cold Water Extension=19 1/8"; Cold Water NPT=2"; Cold Water Radius=1"; Control Panel Extension=25 1/8"; Drain Extension=22"; Drain NPT=1"; Drain Radius=1/2"; Enclosure Location=9 3/4"; Energy Extension=23 1/8"; FC OAL=28 3/8"; Flat Side Distance=34"; Flue Collector Extension=5 1/4"; Flue Diameter=5"; Flue Location=25 3/4"; Flue Radius=2 1/2"; Front Skid Extension=55 1/8"; Height to Cold Inlet=14 13/16"; Height to Drain=1 7/8"; Height to Energy=26 1/2"; Height to Hot Outlet=50 7/8"; Height to Relief=57 7/8"; Hot Outlet Angle=0.00°; Hot Water Extension=19 1/8"; Hot Water NPT=2"; Hot Water Radius=1"; Input Btu/h=399000; Input gph Fuel Oil=2.8; Rear Skid Extension=18 1/8"; Recovery Rate 40F to 140F=400 gph; Relief Extension=21 1/8"; Skid Center Dist=8 1/2"; Skid Length=37"; Skid Spacing=17"; Unit Height=69"; Unit Radius=18 1/8"
- 1000 L 150A-TPO: Air Inlet Diameter=8"; Air Inlet Radius=4"; Cold Water Extension=19 1/8"; Cold Water NPT=2"; Cold Water Radius=1"; Control Panel Extension=25 1/8"; Drain Extension=22"; Drain NPT=1"; Drain Radius=1/2"; Enclosure Location=6"; Energy Extension=37 1/8"; FC OAL=45 3/8"; Flat Side Distance=34"; Flue Collector Extension=8 1/4"; Flue Diameter=8"; Flue Location=41 1/4"; Flue Radius=4"; Front Skid Extension=55 1/8"; Height to Cold Inlet=14 13/16"; Height to Drain=1 7/8"; Height to Energy=26 1/2"; Height to Hot Outlet=44 7/8"; Height to Relief=51 7/8"; Hot Outlet Angle=0.00°; Hot Water Extension=19 1/8"; Hot Water NPT=2"; Hot Water Radius=1"; Input Btu/h=800000; Input gph Fuel Oil=5.7; Rear Skid Extension=18 1/8"; Recovery Rate 40F to 140F=800 gph; Relief Extension=21 1/8"; Skid Center Dist=8 1/2"; Skid Length=37"; Skid Spacing=17"; Unit Height=63"; Unit Radius=18 1/8"
- 750 L 150A-TPO: Air Inlet Diameter=6"; Air Inlet Radius=3"; Cold Water Extension=19 1/8"; Cold Water NPT=2"; Cold Water Radius=1"; Control Panel Extension=25 1/8"; Drain Extension=22"; Drain NPT=1"; Drain Radius=1/2"; Enclosure Location=6"; Energy Extension=37 1/8"; FC OAL=45 3/8"; Flat Side Distance=34"; Flue Collector Extension=8 1/4"; Flue Diameter=6"; Flue Location=41 1/4"; Flue Radius=3"; Front Skid Extension=55 1/8"; Height to Cold Inlet=14 13/16"; Height to Drain=1 7/8"; Height to Energy=26 1/2"; Height to Hot Outlet=44 7/8"; Height to Relief=51 7/8"; Hot Outlet Angle=0.00°; Hot Water Extension=19 1/8"; Hot Water NPT=2"; Hot Water Radius=1"; Input Btu/h=600000; Input gph Fuel Oil=4.3; Rear Skid Extension=18 1/8"; Recovery Rate 40F to 140F=600 gph; Relief Extension=21 1/8"; Skid Center Dist=8 1/2"; Skid Length=37"; Skid Spacing=17"; Unit Height=63"; Unit Radius=18 1/8"
- 500 L 150A-TPO: Air Inlet Diameter=5"; Air Inlet Radius=2 1/2"; Cold Water Extension=19 1/8"; Cold Water NPT=2"; Cold Water Radius=1"; Control Panel Extension=25 1/8"; Drain Extension=22"; Drain NPT=1"; Drain Radius=1/2"; Enclosure Location=6"; Energy Extension=23 1/8"; FC OAL=28 3/8"; Flat Side Distance=34"; Flue Collector Extension=5 1/4"; Flue Diameter=5"; Flue Location=25 3/4"; Flue Radius=2 1/2"; Front Skid Extension=55 1/8"; Height to Cold Inlet=14 13/16"; Height to Drain=1 7/8"; Height to Energy=26 1/2"; Height to Hot Outlet=44 7/8"; Height to Relief=51 7/8"; Hot Outlet Angle=0.00°; Hot Water Extension=19 1/8"; Hot Water NPT=2"; Hot Water Radius=1"; Input Btu/h=399000; Input gph Fuel Oil=2.8; Rear Skid Extension=18 1/8"; Recovery Rate 40F to 140F=400 gph; Relief Extension=21 1/8"; Skid Center Dist=8 1/2"; Skid Length=37"; Skid Spacing=17"; Unit Height=63"; Unit Radius=18 1/8"

note: column(s) folded — value = type name in every type: Model

## geometry (parser evidence)
native form markers: Blend x2, Sweep x3
no freeform markers — native parametric forms only
